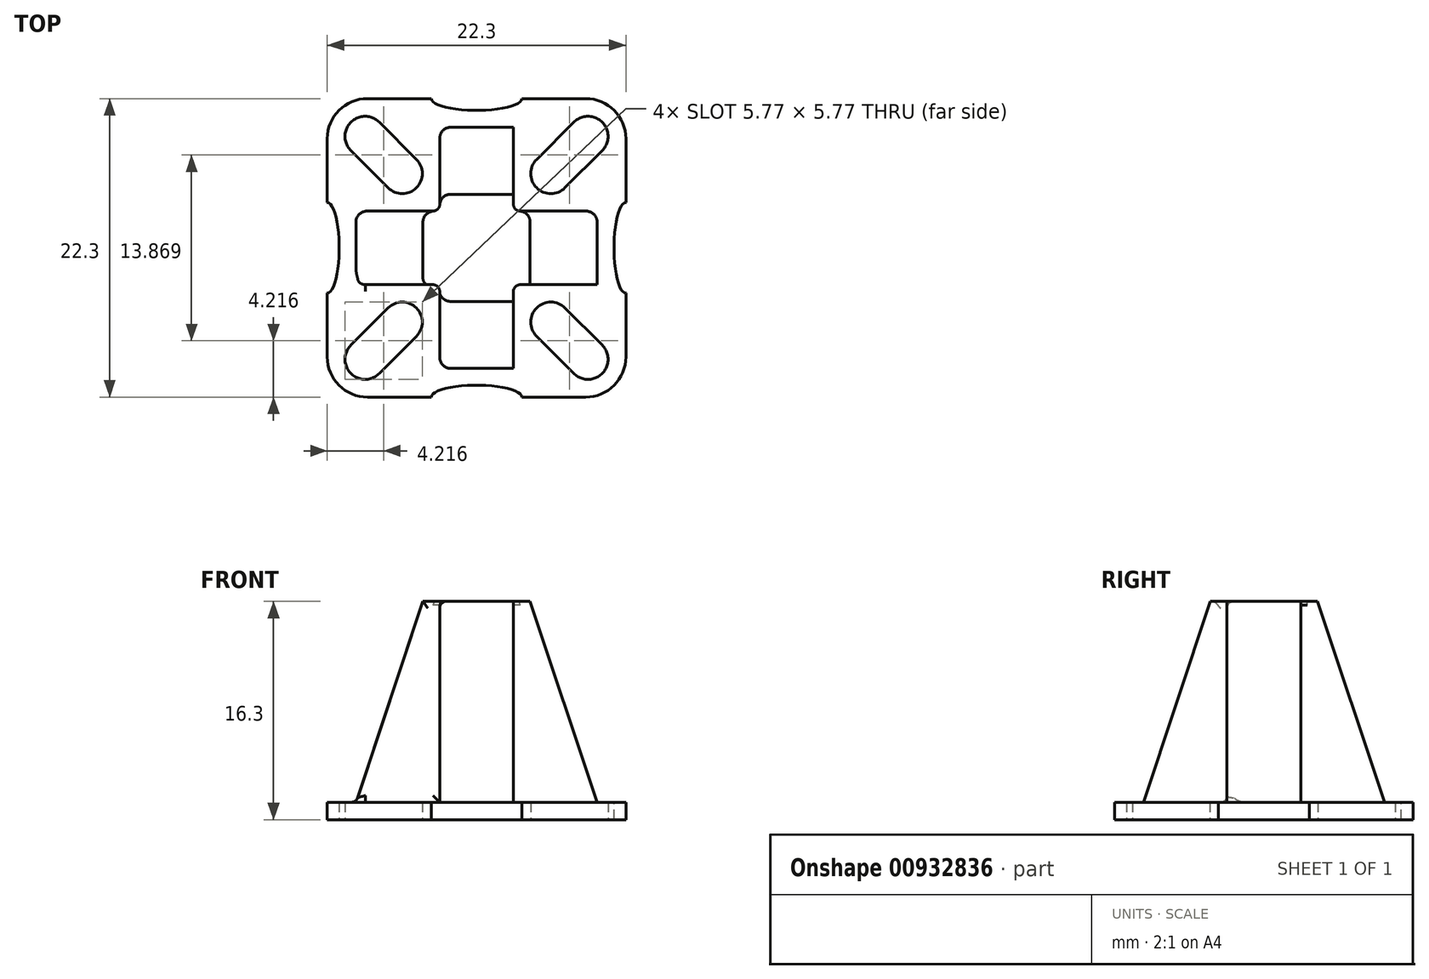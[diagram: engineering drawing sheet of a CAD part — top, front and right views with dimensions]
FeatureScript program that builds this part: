
annotation { "Feature Type Name" : "Feature", "Feature Type Description" : "" }
export const myFeature = defineFeature(function(context is Context, id is Id, definition is map)
    precondition{}
    {
        {
            var Q0;
            Q0=qCreatedBy(makeId("Top.planeOp"),FACE);
            var sketch = newSketch(context, id + "F0", { "sketchPlane" : qUnion([Q0])});
            skLineSegment(sketch, "E0.bottom", {"start": v(11.15, -11.15) * mm, "end": v(-11.15, -11.15) * mm});
            skLineSegment(sketch, "E0.top", {"start": v(11.15, 11.15) * mm, "end": v(-11.15, 11.15) * mm});
            skLineSegment(sketch, "E0.left", {"start": v(11.15, -11.15) * mm, "end": v(11.15, 11.15) * mm});
            skLineSegment(sketch, "E0.right", {"start": v(-11.15, -11.15) * mm, "end": v(-11.15, 11.15) * mm});
            skPoint(sketch, "E0.middle", {"position": v(0, 0) * mm});
            skSolve(sketch);
        }
        {
            var Q0;
            Q0 = qSketchRegion(id + "F0", true);
            extrude(context, id + "F1", {"entities" : qUnion([Q0]), "depth" : 1.3 * mm, "offsetDistance" : 25 * mm});
        }
        {
            var Q0;
            Q0=makeQuery(id+"F1.opExtrude","CAP_FACE",FACE,{"disambiguationData":[OSD([sQuery(id+"F0.wireOp",EDGE,"E0.bottom"),sQuery(id+"F0.wireOp",EDGE,"E0.top"),sQuery(id+"F0.wireOp",EDGE,"E0.left"),sQuery(id+"F0.wireOp",EDGE,"E0.right")])],"isStart":false});
            var sketch = newSketch(context, id + "F2", { "sketchPlane" : qUnion([Q0])});
            skLineSegment(sketch, "E1", {"start": v(-11.15, 0) * mm, "end": v(11.15, 0) * mm});
            skLineSegment(sketch, "E2", {"start": v(0, 11.15) * mm, "end": v(0, -11.15) * mm});
            skLineSegment(sketch, "E3.bottom", {"start": v(9, -2.75) * mm, "end": v(-9, -2.75) * mm});
            skLineSegment(sketch, "E3.top", {"start": v(9, 2.75) * mm, "end": v(-9, 2.75) * mm});
            skLineSegment(sketch, "E3.left", {"start": v(9, -2.75) * mm, "end": v(9, 2.75) * mm});
            skLineSegment(sketch, "E3.right", {"start": v(-9, -2.75) * mm, "end": v(-9, 2.75) * mm});
            skPoint(sketch, "E3.middle", {"position": v(0, 0) * mm});
            skLineSegment(sketch, "E4.bottom", {"start": v(2.75, -9) * mm, "end": v(-2.75, -9) * mm});
            skLineSegment(sketch, "E4.top", {"start": v(2.75, 9) * mm, "end": v(-2.75, 9) * mm});
            skLineSegment(sketch, "E4.left", {"start": v(2.75, -9) * mm, "end": v(2.75, 9) * mm});
            skLineSegment(sketch, "E4.right", {"start": v(-2.75, -9) * mm, "end": v(-2.75, 9) * mm});
            skSolve(sketch);
        }
        {
            var Q0;
            Q0 = qSketchRegion(id + "F2", true);
            extrude(context, id + "F3", {"entities" : qUnion([Q0]), "operationType" : NewBodyOperationType.ADD, "depth" : 15 * mm, "offsetDistance" : 25 * mm});
        }
        {
            var Q0;
            {var subQ0=sQuery(id+"F2.wireOp",EDGE,"E3.bottom");Q0=makeQuery(id+"F3.opExtrude","SWEPT_FACE",FACE,{"disambiguationData":[OSD([subQ0]),TDD([makeQuery(id+"F2.imprint","IMPRINT",EDGE,{"disambiguationData":[TD([[makeQuery(id+"F2.imprint","INTERSECT",VERTEX,{"derivedFrom":[subQ0,sQuery(id+"F2.wireOp",EDGE,"E3.right")]}),1.0]])],"derivedFrom":subQ0})])]});}
            var sketch = newSketch(context, id + "F4", { "sketchPlane" : qUnion([Q0])});
            skLineSegment(sketch, "E5", {"start": v(-9, 1.3) * mm, "end": v(-4, 16.3) * mm});
            skSolve(sketch);
        }
        {
            var Q0;
            {var subQ0=sQuery(id+"F4.wireOp",EDGE,"E5");Q0=makeQuery(id+"F4.imprint","IMPRINT",FACE,{"disambiguationData":[TD([[makeQuery(id+"F4.imprint","IMPRINT",EDGE,{"derivedFrom":subQ0}),1.0]])]});}
            extrude(context, id + "F5", {"entities" : qUnion([Q0]), "operationType" : NewBodyOperationType.REMOVE, "oppositeDirection" : true, "depth" : 6.2 * mm, "offsetDistance" : 25 * mm});
        }
        {
            var Q0;
            {var subQ0=sQuery(id+"F2.wireOp",EDGE,"E3.bottom");Q0=makeQuery(id+"F3.opExtrude","SWEPT_FACE",FACE,{"disambiguationData":[OSD([subQ0]),TDD([makeQuery(id+"F2.imprint","IMPRINT",EDGE,{"disambiguationData":[TD([[makeQuery(id+"F2.imprint","INTERSECT",VERTEX,{"derivedFrom":[subQ0,sQuery(id+"F2.wireOp",EDGE,"E3.left")]}),-1.0]])],"derivedFrom":subQ0})])]});}
            var sketch = newSketch(context, id + "F6", { "sketchPlane" : qUnion([Q0])});
            skLineSegment(sketch, "E6", {"start": v(9, 1.3) * mm, "end": v(4, 16.3) * mm});
            skSolve(sketch);
        }
        {
            var Q0;
            {var subQ0=sQuery(id+"F6.wireOp",EDGE,"E6");Q0=makeQuery(id+"F6.imprint","IMPRINT",FACE,{"disambiguationData":[TD([[makeQuery(id+"F6.imprint","IMPRINT",EDGE,{"derivedFrom":subQ0}),-1.0]])]});}
            extrude(context, id + "F7", {"entities" : qUnion([Q0]), "operationType" : NewBodyOperationType.REMOVE, "oppositeDirection" : true, "depth" : 6.1 * mm, "offsetDistance" : 25 * mm});
        }
        {
            var Q0;
            {var subQ0=sQuery(id+"F2.wireOp",EDGE,"E4.left");Q0=makeQuery(id+"F3.opExtrude","SWEPT_FACE",FACE,{"disambiguationData":[OSD([subQ0]),TDD([makeQuery(id+"F2.imprint","IMPRINT",EDGE,{"disambiguationData":[TD([[makeQuery(id+"F2.imprint","INTERSECT",VERTEX,{"derivedFrom":[sQuery(id+"F2.wireOp",EDGE,"E4.bottom"),subQ0]}),-1.0]])],"derivedFrom":subQ0})])]});}
            var sketch = newSketch(context, id + "F8", { "sketchPlane" : qUnion([Q0])});
            skLineSegment(sketch, "E7", {"start": v(-9, 1.3) * mm, "end": v(-4, 16.3) * mm});
            skSolve(sketch);
        }
        {
            var Q0;
            {var subQ0=sQuery(id+"F8.wireOp",EDGE,"E7");Q0=makeQuery(id+"F8.imprint","IMPRINT",FACE,{"disambiguationData":[TD([[makeQuery(id+"F8.imprint","IMPRINT",EDGE,{"derivedFrom":subQ0}),1.0]])]});}
            extrude(context, id + "F9", {"entities" : qUnion([Q0]), "operationType" : NewBodyOperationType.REMOVE, "oppositeDirection" : true, "depth" : 6.3 * mm, "offsetDistance" : 25 * mm});
        }
        {
            var Q0;
            {var subQ0=sQuery(id+"F2.wireOp",EDGE,"E4.left");Q0=makeQuery(id+"F3.opExtrude","SWEPT_FACE",FACE,{"disambiguationData":[OSD([subQ0]),TDD([makeQuery(id+"F2.imprint","IMPRINT",EDGE,{"disambiguationData":[TD([[makeQuery(id+"F2.imprint","INTERSECT",VERTEX,{"derivedFrom":[sQuery(id+"F2.wireOp",EDGE,"E4.top"),subQ0]}),1.0]])],"derivedFrom":subQ0})])]});}
            var sketch = newSketch(context, id + "F10", { "sketchPlane" : qUnion([Q0])});
            skLineSegment(sketch, "E8", {"start": v(9, 1.3) * mm, "end": v(4, 16.3) * mm});
            skSolve(sketch);
        }
        {
            var Q0;
            {var subQ0=sQuery(id+"F10.wireOp",EDGE,"E8");Q0=makeQuery(id+"F10.imprint","IMPRINT",FACE,{"disambiguationData":[TD([[makeQuery(id+"F10.imprint","IMPRINT",EDGE,{"derivedFrom":subQ0}),-1.0]])]});}
            extrude(context, id + "F11", {"entities" : qUnion([Q0]), "operationType" : NewBodyOperationType.REMOVE, "oppositeDirection" : true, "depth" : 6.1 * mm, "offsetDistance" : 25 * mm});
        }
        {
            var Q0;
            Q0=makeQuery(id+"F1.opExtrude","CAP_FACE",FACE,{"disambiguationData":[OSD([sQuery(id+"F0.wireOp",EDGE,"E0.bottom"),sQuery(id+"F0.wireOp",EDGE,"E0.top"),sQuery(id+"F0.wireOp",EDGE,"E0.left"),sQuery(id+"F0.wireOp",EDGE,"E0.right")])],"isStart":true});
            var sketch = newSketch(context, id + "F12", { "sketchPlane" : qUnion([Q0])});
            skLineSegment(sketch, "E9", {"start": v(-11.15, 11.15) * mm, "end": v(11.15, -11.15) * mm, "construction": true});
            skLineSegment(sketch, "E10", {"start": v(11.15, 11.15) * mm, "end": v(-11.15, -11.15) * mm, "construction": true});
            skCircle(sketch, "E11", {"center": v(8.32, 8.32) * mm, "radius": 1.5 * mm});
            skCircle(sketch, "E12", {"center": v(5.55, 5.55) * mm, "radius": 1.5 * mm});
            skLineSegment(sketch, "E13", {"start": v(5.55, 5.55) * mm, "end": v(6.6, 4.49) * mm, "construction": true});
            skLineSegment(sketch, "E14", {"start": v(8.32, 8.32) * mm, "end": v(9.38, 7.26) * mm, "construction": true});
            skLineSegment(sketch, "E15", {"start": v(5.55, 5.55) * mm, "end": v(4.49, 6.6) * mm, "construction": true});
            skLineSegment(sketch, "E16", {"start": v(8.32, 8.32) * mm, "end": v(7.26, 9.38) * mm, "construction": true});
            skLineSegment(sketch, "E17", {"start": v(9.38, 7.26) * mm, "end": v(6.6, 4.49) * mm});
            skLineSegment(sketch, "E18", {"start": v(7.26, 9.38) * mm, "end": v(4.49, 6.6) * mm});
            skCircle(sketch, "E19.1.0", {"center": v(5.55, -5.55) * mm, "radius": 1.5 * mm});
            skCircle(sketch, "E19.1.1", {"center": v(8.32, -8.32) * mm, "radius": 1.5 * mm});
            skLineSegment(sketch, "E19.1.2", {"start": v(9.38, -7.26) * mm, "end": v(6.6, -4.49) * mm});
            skLineSegment(sketch, "E19.1.3", {"start": v(7.26, -9.38) * mm, "end": v(4.49, -6.6) * mm});
            skCircle(sketch, "E19.2.0", {"center": v(-5.55, -5.55) * mm, "radius": 1.5 * mm});
            skCircle(sketch, "E19.2.1", {"center": v(-8.32, -8.32) * mm, "radius": 1.5 * mm});
            skLineSegment(sketch, "E19.2.2", {"start": v(-7.26, -9.38) * mm, "end": v(-4.49, -6.6) * mm});
            skLineSegment(sketch, "E19.2.3", {"start": v(-9.38, -7.26) * mm, "end": v(-6.6, -4.49) * mm});
            skCircle(sketch, "E19.3.0", {"center": v(-5.55, 5.55) * mm, "radius": 1.5 * mm});
            skCircle(sketch, "E19.3.1", {"center": v(-8.32, 8.32) * mm, "radius": 1.5 * mm});
            skLineSegment(sketch, "E19.3.2", {"start": v(-9.38, 7.26) * mm, "end": v(-6.6, 4.49) * mm});
            skLineSegment(sketch, "E19.3.3", {"start": v(-7.26, 9.38) * mm, "end": v(-4.49, 6.6) * mm});
            skPoint(sketch, "E19.center", {"position": v(0, 0) * mm});
            skLineSegment(sketch, "E19.anchor1", {"start": v(0, 0) * mm, "end": v(5.55, 5.55) * mm, "construction": true});
            skLineSegment(sketch, "E19.anchor2", {"start": v(0, 0) * mm, "end": v(-5.55, 5.55) * mm, "construction": true});
            skEllipse(sketch, "E20", {"center": v(0, 11.15) * mm, "majorRadius": 3.39 * mm, "minorRadius": 0.9 * mm, "majorAxis": v(-1, 0)});
            skEllipse(sketch, "E21.1.0", {"center": v(11.15, 0) * mm, "majorRadius": 3.39 * mm, "minorRadius": 0.9 * mm, "majorAxis": v(0, 1)});
            skEllipse(sketch, "E21.2.0", {"center": v(0, -11.15) * mm, "majorRadius": 3.39 * mm, "minorRadius": 0.9 * mm, "majorAxis": v(1, 0)});
            skEllipse(sketch, "E21.3.0", {"center": v(-11.15, 0) * mm, "majorRadius": 3.39 * mm, "minorRadius": 0.9 * mm, "majorAxis": v(0, -1)});
            skLineSegment(sketch, "E21.anchor1", {"start": v(0, 0) * mm, "end": v(0, 11.15) * mm, "construction": true});
            skLineSegment(sketch, "E21.anchor2", {"start": v(0, 0) * mm, "end": v(-11.15, 0) * mm, "construction": true});
            skSolve(sketch);
        }
        {
            var Q0;
            Q0 = qSketchRegion(id + "F12", true);
            extrude(context, id + "F13", {"entities" : qUnion([Q0]), "operationType" : NewBodyOperationType.REMOVE, "oppositeDirection" : true, "depth" : 1.6 * mm, "offsetDistance" : 25 * mm});
        }
        {
            var Q0;
            Q0=makeQuery(id+"F1.opExtrude","SWEPT_EDGE",EDGE,{"disambiguationData":[OSD([sQuery(id+"F0.wireOp",EDGE,"E0.top"),sQuery(id+"F0.wireOp",EDGE,"E0.left")])]});
            var Q1;
            Q1=makeQuery(id+"F1.opExtrude","SWEPT_EDGE",EDGE,{"disambiguationData":[OSD([sQuery(id+"F0.wireOp",EDGE,"E0.top"),sQuery(id+"F0.wireOp",EDGE,"E0.right")])]});
            var Q2;
            Q2=makeQuery(id+"F1.opExtrude","SWEPT_EDGE",EDGE,{"disambiguationData":[OSD([sQuery(id+"F0.wireOp",EDGE,"E0.bottom"),sQuery(id+"F0.wireOp",EDGE,"E0.right")])]});
            var Q3;
            Q3=makeQuery(id+"F1.opExtrude","SWEPT_EDGE",EDGE,{"disambiguationData":[OSD([sQuery(id+"F0.wireOp",EDGE,"E0.bottom"),sQuery(id+"F0.wireOp",EDGE,"E0.left")])]});
            fillet(context, id + "F14", {"entities" : qUnion([Q0, Q1, Q2, Q3]), "radius" : 3 * mm, "tangentPropagation" : true, "allowEdgeOverflow" : false});
        }
        {
            var Q0;
            Q0=makeQuery(id+"F7.boolean.opBoolean","COPY",EDGE,{"derivedFrom":makeQuery(id+"F7.opExtrude","CAP_EDGE",EDGE,{"disambiguationData":[OSD([sQuery(id+"F6.wireOp",EDGE,"E6")])],"isStart":true})});
            var Q1;
            Q1=makeQuery(id+"F9.boolean.opBoolean","COPY",EDGE,{"derivedFrom":makeQuery(id+"F9.opExtrude","CAP_EDGE",EDGE,{"disambiguationData":[OSD([sQuery(id+"F8.wireOp",EDGE,"E7")])],"isStart":true})});
            var Q2;
            {var subQ0=sQuery(id+"F2.wireOp",EDGE,"E3.top");Q2=makeQuery(id+"F7.boolean.opBoolean","INTERSECT",EDGE,{"derivedFrom":[makeQuery(id+"F3.opExtrude","SWEPT_FACE",FACE,{"disambiguationData":[OSD([subQ0]),TDD([makeQuery(id+"F2.imprint","IMPRINT",EDGE,{"disambiguationData":[TD([[makeQuery(id+"F2.imprint","INTERSECT",VERTEX,{"derivedFrom":[subQ0,sQuery(id+"F2.wireOp",EDGE,"E3.left")]}),-1.0]])],"derivedFrom":subQ0})])]}),makeQuery(id+"F7.opExtrude","SWEPT_FACE",FACE,{"disambiguationData":[OSD([sQuery(id+"F6.wireOp",EDGE,"E6")])]})]});}
            var Q3;
            Q3=makeQuery(id+"F11.boolean.opBoolean","COPY",EDGE,{"derivedFrom":makeQuery(id+"F11.opExtrude","CAP_EDGE",EDGE,{"disambiguationData":[OSD([sQuery(id+"F10.wireOp",EDGE,"E8")])],"isStart":true})});
            var Q4;
            {var subQ0=sQuery(id+"F2.wireOp",EDGE,"E4.right");Q4=makeQuery(id+"F11.boolean.opBoolean","INTERSECT",EDGE,{"derivedFrom":[makeQuery(id+"F3.opExtrude","SWEPT_FACE",FACE,{"disambiguationData":[OSD([subQ0]),TDD([makeQuery(id+"F2.imprint","IMPRINT",EDGE,{"disambiguationData":[TD([[makeQuery(id+"F2.imprint","INTERSECT",VERTEX,{"derivedFrom":[sQuery(id+"F2.wireOp",EDGE,"E4.top"),subQ0]}),1.0]])],"derivedFrom":subQ0})])]}),makeQuery(id+"F11.opExtrude","SWEPT_FACE",FACE,{"disambiguationData":[OSD([sQuery(id+"F10.wireOp",EDGE,"E8")])]})]});}
            var Q5;
            {var subQ0=sQuery(id+"F2.wireOp",EDGE,"E3.top");Q5=makeQuery(id+"F5.boolean.opBoolean","INTERSECT",EDGE,{"derivedFrom":[makeQuery(id+"F3.opExtrude","SWEPT_FACE",FACE,{"disambiguationData":[OSD([subQ0]),TDD([makeQuery(id+"F2.imprint","IMPRINT",EDGE,{"disambiguationData":[TD([[makeQuery(id+"F2.imprint","INTERSECT",VERTEX,{"derivedFrom":[subQ0,sQuery(id+"F2.wireOp",EDGE,"E3.right")]}),1.0]])],"derivedFrom":subQ0})])]}),makeQuery(id+"F5.opExtrude","SWEPT_FACE",FACE,{"disambiguationData":[OSD([sQuery(id+"F4.wireOp",EDGE,"E5")])]})]});}
            var Q6;
            Q6=makeQuery(id+"F5.boolean.opBoolean","COPY",EDGE,{"derivedFrom":makeQuery(id+"F5.opExtrude","CAP_EDGE",EDGE,{"disambiguationData":[OSD([sQuery(id+"F4.wireOp",EDGE,"E5")])],"isStart":true})});
            var Q7;
            {var subQ0=sQuery(id+"F2.wireOp",EDGE,"E4.right");Q7=makeQuery(id+"F9.boolean.opBoolean","INTERSECT",EDGE,{"derivedFrom":[makeQuery(id+"F3.opExtrude","SWEPT_FACE",FACE,{"disambiguationData":[OSD([subQ0]),TDD([makeQuery(id+"F2.imprint","IMPRINT",EDGE,{"disambiguationData":[TD([[makeQuery(id+"F2.imprint","INTERSECT",VERTEX,{"derivedFrom":[sQuery(id+"F2.wireOp",EDGE,"E4.bottom"),subQ0]}),-1.0]])],"derivedFrom":subQ0})])]}),makeQuery(id+"F9.opExtrude","SWEPT_FACE",FACE,{"disambiguationData":[OSD([sQuery(id+"F8.wireOp",EDGE,"E7")])]})]});}
            fillet(context, id + "F15", {"entities" : qUnion([Q0, Q1, Q2, Q3, Q4, Q5, Q6, Q7]), "radius" : 0.8 * mm, "tangentPropagation" : true, "allowEdgeOverflow" : false});
        }
        {
            var Q0;
            Q0=makeQuery(id+"F3.opExtrude","SWEPT_EDGE",EDGE,{"disambiguationData":[OSD([sQuery(id+"F2.wireOp",EDGE,"E3.bottom"),sQuery(id+"F2.wireOp",EDGE,"E4.left")])]});
            var Q1;
            Q1=makeQuery(id+"F3.opExtrude","SWEPT_EDGE",EDGE,{"disambiguationData":[OSD([sQuery(id+"F2.wireOp",EDGE,"E3.top"),sQuery(id+"F2.wireOp",EDGE,"E4.left")])]});
            var Q2;
            Q2=makeQuery(id+"F3.opExtrude","SWEPT_EDGE",EDGE,{"disambiguationData":[OSD([sQuery(id+"F2.wireOp",EDGE,"E3.top"),sQuery(id+"F2.wireOp",EDGE,"E4.right")])]});
            var Q3;
            {var subQ0=sQuery(id+"F2.wireOp",EDGE,"E3.bottom");Q3=makeQuery(id+"F3.opExtrude","SWEPT_FACE",FACE,{"disambiguationData":[OSD([subQ0]),TDD([makeQuery(id+"F2.imprint","IMPRINT",EDGE,{"disambiguationData":[TD([[makeQuery(id+"F2.imprint","INTERSECT",VERTEX,{"derivedFrom":[subQ0,sQuery(id+"F2.wireOp",EDGE,"E3.right")]}),1.0]])],"derivedFrom":subQ0})])]});}
            var Q4;
            {var subQ0=sQuery(id+"F2.wireOp",EDGE,"E4.left");Q4=makeQuery(id+"F3.opExtrude","CAP_EDGE",EDGE,{"disambiguationData":[OSD([subQ0]),TDD([makeQuery(id+"F2.imprint","IMPRINT",EDGE,{"disambiguationData":[TD([[makeQuery(id+"F2.imprint","INTERSECT",VERTEX,{"derivedFrom":[sQuery(id+"F2.wireOp",EDGE,"E4.top"),subQ0]}),1.0]])],"derivedFrom":subQ0})])],"isStart":true});}
            var Q5;
            {var subQ0=sQuery(id+"F2.wireOp",EDGE,"E3.top");Q5=makeQuery(id+"F3.opExtrude","CAP_EDGE",EDGE,{"disambiguationData":[OSD([subQ0]),TDD([makeQuery(id+"F2.imprint","IMPRINT",EDGE,{"disambiguationData":[TD([[makeQuery(id+"F2.imprint","INTERSECT",VERTEX,{"derivedFrom":[subQ0,sQuery(id+"F2.wireOp",EDGE,"E3.left")]}),-1.0]])],"derivedFrom":subQ0})])],"isStart":true});}
            var Q6;
            {var subQ0=sQuery(id+"F2.wireOp",EDGE,"E4.left");Q6=makeQuery(id+"F3.opExtrude","CAP_EDGE",EDGE,{"disambiguationData":[OSD([subQ0]),TDD([makeQuery(id+"F2.imprint","IMPRINT",EDGE,{"disambiguationData":[TD([[makeQuery(id+"F2.imprint","INTERSECT",VERTEX,{"derivedFrom":[sQuery(id+"F2.wireOp",EDGE,"E4.bottom"),subQ0]}),-1.0]])],"derivedFrom":subQ0})])],"isStart":true});}
            fillet(context, id + "F16", {"entities" : qUnion([Q0, Q1, Q2, Q3, Q4, Q5, Q6]), "radius" : 0.5 * mm, "tangentPropagation" : true, "allowEdgeOverflow" : false});
        }
    });
